# Revit family: 0047692 Lighting Fixture_Sylvania_Sylproof Superia LED_Surface Mounted
name_source: partatom
category: Lighting Fixtures
revit_build: Autodesk Revit 2015 (Build: 20140606_1530(x64)
units: mm (PartAtom-declared; Revit-internal decimal feet)

## types (1)
- SYLPROOF SUPERIA LED 1565MM TWIN NW
    Apparent Load = 79 VA
    Assembly Code = D5020200
    Body Material = Polycarbonate_Body_Sylvania_Brite White
    Bracket-Diffuser Material = <By Category>
    Bracket-Mounting Material = <By Category>
    CRI ( Ra ) = 85
    Catalog Number = 0047692 SYLPROOF SUPERIA LED 1565MM TWIN NW
    Color Filter = 16777215
    Default Elevation = 0 mm  [stored 0 ft]
    Description = Weatherproof LED luminaire achieving up to 6,880lm (86lm/W); Linear prisms designed to optimise light output and to reduce glare;Extra long life with 50,000 hours; LED technology provides energy efficient solution and reduced maintenance costs.
    Diffuser Brackets Length = 1405 mm  [stored 4.60958 ft]
    Diffuser Material = Polycarbonate_Diffuser_Sylvania_Clear
    Dimming Lamp Color Temperature Shift = <None>
    Emit Shape Visible in Rendering = No
    Emit from Rectangle Length = 1545 mm
    Emit from Rectangle Width = 110 mm  [stored 0.360892 ft]
    Height = 97 mm  [stored 0.318241 ft]
    Housing ( Degree ) = 850 C
    IP rating = 65
    LOR Light Output Ratio ( % ) = 100 %
    Lamp = 79W LED
    Lamp - Single = No
    Lamp - Twin = Yes
    Lamp Comments = Integrated LED
    Lamp Material = Acrylic High Luminance Glass_Lamp_Sylvania_White
    Length = 1565 mm  [stored 5.13451 ft]
    Length Help = 1505 mm  [stored 4.93766 ft]
    Manufacturer = Feilo-Sylvania Group
    Model = SYLPROOF SUPERIA LED 1565MM TWIN NW
    Mounting Brackets Length = 940 mm  [stored 3.08399 ft]
    Mounting Brackets Width = 54 mm  [stored 0.177165 ft]
    Number of Diffuser Brackets = 6
    Photometric Web File = 0047692_SYLPROOFSUPERIALED80W4KNW-164268.ies
    Product Family = Sylproof Susperia LED
    Side Void Width = 70 mm  [stored 0.229659 ft]
    Tilt Angle = -90.00°
    Voltage = 240 V
    Voltage Comments = UNV (Universal Voltage; 220-240 Volt)
    Weight = 3.30 kg
    Width = 138 mm  [stored 0.452756 ft]
    Width Help = 70 mm  [stored 0.229659 ft]

note: [stored X ft] marks values corroborated as IEEE doubles in the binary element streams (Revit-internal decimal feet)

## geometry (parser evidence)
native form markers: Blend x5, Sweep x13
no freeform markers — native parametric forms only
